# Revit family: revitupgrade
name_source: partatom
category: Furniture
units: mm (PartAtom-declared; Revit-internal decimal feet)

## family parameters
Always vertical = Yes
Cut with Voids When Loaded = No
Enable Cutting in Views = No
OmniClass Number = 23.40.70.14.64.11
OmniClass Title = Office Furniture
Render Appearance Source = Family Geometry
Room Calculation Point = No
Shared = No
Work Plane-Based = No

## types (2) — shared parameters
Assembly Code = E2020200
Description = Just like learning, furniture shouldn’t be forced.  Flowform® is refreshing in that way.  They feature deliberate organic shapes with soft radii and rounded edging.
Glide = SmithSystem_Plastic_Black
Manufacturer = Smith System
Release Date = June 2023
URL = https://www.steelcase.com
zero-valued in all types: Default Elevation

## per-type parameters (varying)
| type | LargeBench | SmallBench | Style Number(s) |
| Small Bench | No | Yes | SMSFS55002 |
| Large Bench | Yes | No | SMSFS55003 |

## geometry (parser evidence)
native form markers: Sweep x3
no freeform markers — native parametric forms only
